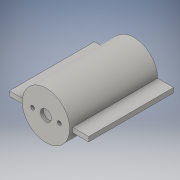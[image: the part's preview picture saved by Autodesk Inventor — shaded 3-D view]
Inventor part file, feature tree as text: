
AUTODESK INVENTOR PART (.ipt)
format: ipt  version: 2016 SP1 (Build 200210100, 210)  size: 120,320 bytes
history: native  units: in
note: dims shown in document units (in); Inventor stores cm internally (conversion verified against a paired STEP export)
features: other x3, sketch x3
ambient origin geometry x8: Origin, YZ Plane, XZ Plane, XY Plane, X Axis, Y Axis, Z Axis, Center Point
bodies: Solid1 (feature_tree)
feature tree (6):
  other  "Attachment2.ipt"
  other  "Solid2::Attachment2.ipt"
  other  "TaggingFeature1"
  sketch  "Sketch1"  dims[d0=0.3937in]
  sketch  "Sketch2"
  sketch  "Sketch3"
